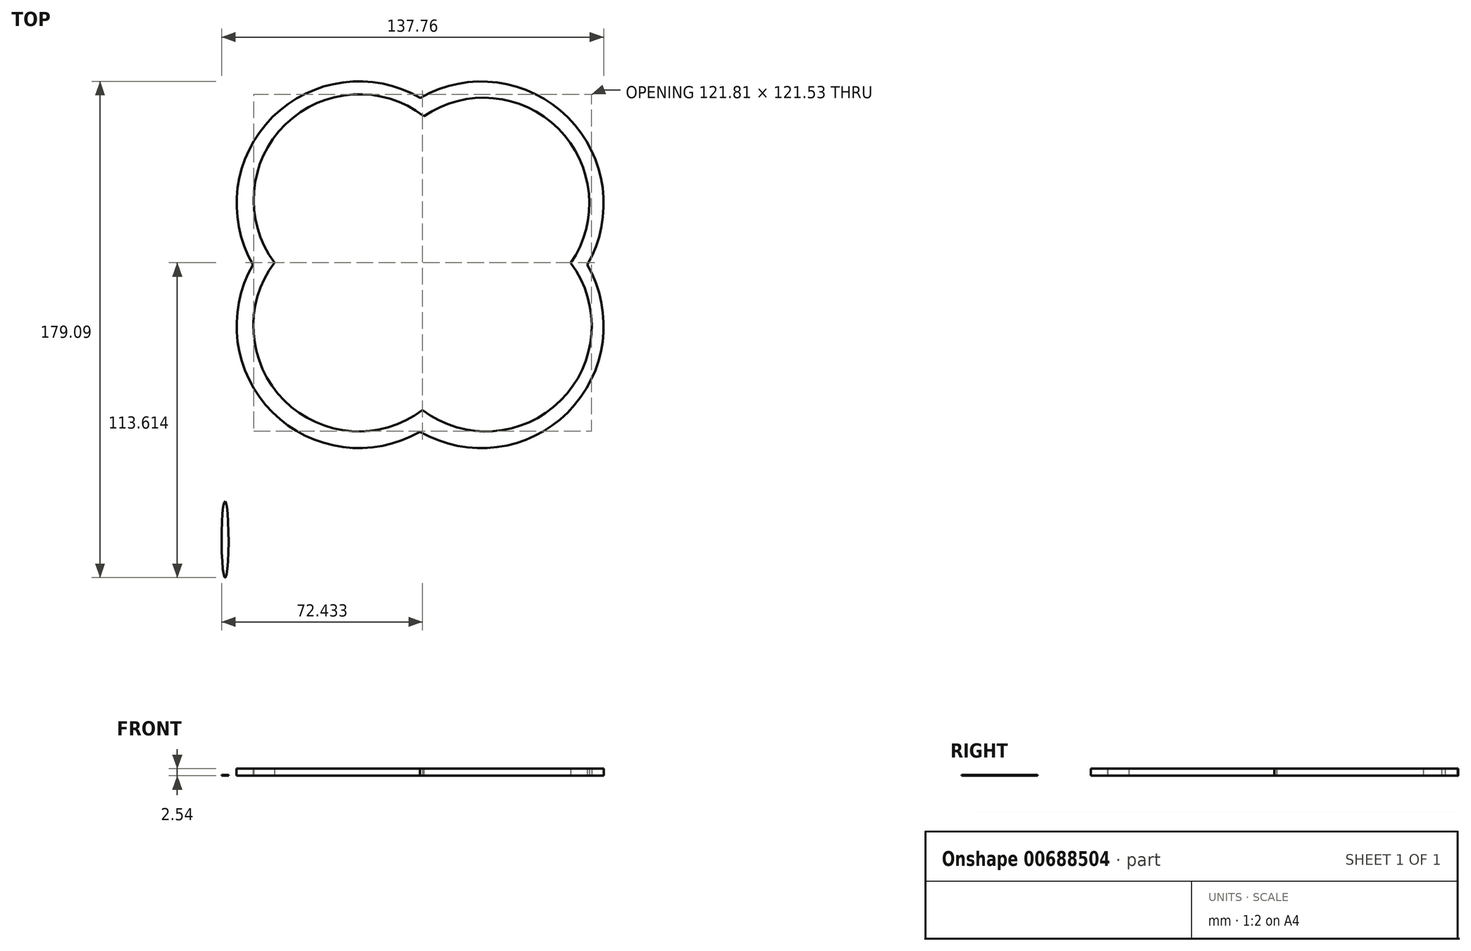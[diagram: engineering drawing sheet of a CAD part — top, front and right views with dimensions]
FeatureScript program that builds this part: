
annotation { "Feature Type Name" : "Feature", "Feature Type Description" : "" }
export const myFeature = defineFeature(function(context is Context, id is Id, definition is map)
    precondition{}
    {
        {
            var Q0;
            Q0=qCreatedBy(makeId("Top.planeOp"),FACE);
            var sketch = newSketch(context, id + "F0", { "sketchPlane" : qUnion([Q0])});
            skCircle(sketch, "E0", {"center": v(0, 44.12) * mm, "radius": 44.12 * mm});
            skCircle(sketch, "E1", {"center": v(44.12, 44.07) * mm, "radius": 44.12 * mm});
            skCircle(sketch, "E2", {"center": v(44.12, -0.05) * mm, "radius": 44.12 * mm});
            skCircle(sketch, "E3", {"center": v(0, 0) * mm, "radius": 44.12 * mm});
            skSolve(sketch);
        }
        {
            var Q0;
            {var subQ0=sQuery(id+"F0.wireOp",EDGE,"E3");var subQ1=sQuery(id+"F0.wireOp",EDGE,"E0");var subQ2=makeQuery(id+"F0.imprint","INTERSECT",VERTEX,{"disambiguationData":[OD(0.0)],"derivedFrom":[subQ1,subQ0]});Q0=makeQuery(id+"F0.imprint","IMPRINT",FACE,{"disambiguationData":[TD([[makeQuery(id+"F0.imprint","IMPRINT",EDGE,{"disambiguationData":[TD([[subQ2,1.0]])],"derivedFrom":subQ1}),1.0]])]});}
            var Q1;
            {var subQ0=sQuery(id+"F0.wireOp",EDGE,"E3");var subQ1=sQuery(id+"F0.wireOp",EDGE,"E0");var subQ2=makeQuery(id+"F0.imprint","INTERSECT",VERTEX,{"disambiguationData":[OD(0.0)],"derivedFrom":[subQ1,subQ0]});Q1=makeQuery(id+"F0.imprint","IMPRINT",FACE,{"disambiguationData":[TD([[makeQuery(id+"F0.imprint","IMPRINT",EDGE,{"disambiguationData":[TD([[subQ2,-1.0]])],"derivedFrom":subQ1}),1.0]])]});}
            var Q2;
            {var subQ0=sQuery(id+"F0.wireOp",EDGE,"E1");var subQ1=sQuery(id+"F0.wireOp",EDGE,"E0");var subQ2=makeQuery(id+"F0.imprint","INTERSECT",VERTEX,{"disambiguationData":[OD(0.0)],"derivedFrom":[subQ1,subQ0]});Q2=makeQuery(id+"F0.imprint","IMPRINT",FACE,{"disambiguationData":[TD([[makeQuery(id+"F0.imprint","IMPRINT",EDGE,{"disambiguationData":[TD([[subQ2,1.0]])],"derivedFrom":subQ1}),1.0]])]});}
            var Q3;
            {var subQ0=sQuery(id+"F0.wireOp",EDGE,"E3");var subQ1=sQuery(id+"F0.wireOp",EDGE,"E0");var subQ2=makeQuery(id+"F0.imprint","INTERSECT",VERTEX,{"disambiguationData":[OD(0.0)],"derivedFrom":[subQ1,subQ0]});Q3=makeQuery(id+"F0.imprint","IMPRINT",FACE,{"disambiguationData":[TD([[makeQuery(id+"F0.imprint","IMPRINT",EDGE,{"disambiguationData":[TD([[subQ2,-1.0]])],"derivedFrom":subQ1}),-1.0]])]});}
            var Q4;
            {var subQ0=sQuery(id+"F0.wireOp",EDGE,"E2");var subQ1=sQuery(id+"F0.wireOp",EDGE,"E0");var subQ2=makeQuery(id+"F0.imprint","INTERSECT",VERTEX,{"disambiguationData":[OD(0.0)],"derivedFrom":[subQ1,subQ0]});Q4=makeQuery(id+"F0.imprint","IMPRINT",FACE,{"disambiguationData":[TD([[makeQuery(id+"F0.imprint","IMPRINT",EDGE,{"disambiguationData":[TD([[subQ2,-1.0]])],"derivedFrom":subQ1}),-1.0]])]});}
            var Q5;
            {var subQ0=sQuery(id+"F0.wireOp",EDGE,"E2");var subQ1=sQuery(id+"F0.wireOp",EDGE,"E1");var subQ2=makeQuery(id+"F0.imprint","INTERSECT",VERTEX,{"disambiguationData":[OD(0.0)],"derivedFrom":[subQ1,subQ0]});Q5=makeQuery(id+"F0.imprint","IMPRINT",FACE,{"disambiguationData":[TD([[makeQuery(id+"F0.imprint","IMPRINT",EDGE,{"disambiguationData":[TD([[subQ2,1.0]])],"derivedFrom":subQ1}),-1.0]])]});}
            var Q6;
            {var subQ0=sQuery(id+"F0.wireOp",EDGE,"E1");var subQ1=sQuery(id+"F0.wireOp",EDGE,"E0");var subQ2=makeQuery(id+"F0.imprint","INTERSECT",VERTEX,{"disambiguationData":[OD(0.0)],"derivedFrom":[subQ1,subQ0]});Q6=makeQuery(id+"F0.imprint","IMPRINT",FACE,{"disambiguationData":[TD([[makeQuery(id+"F0.imprint","IMPRINT",EDGE,{"disambiguationData":[TD([[subQ2,1.0]])],"derivedFrom":subQ1}),-1.0]])]});}
            var Q7;
            {var subQ0=sQuery(id+"F0.wireOp",EDGE,"E3");var subQ1=sQuery(id+"F0.wireOp",EDGE,"E0");var subQ2=makeQuery(id+"F0.imprint","INTERSECT",VERTEX,{"disambiguationData":[OD(1.0)],"derivedFrom":[subQ1,subQ0]});Q7=makeQuery(id+"F0.imprint","IMPRINT",FACE,{"disambiguationData":[TD([[makeQuery(id+"F0.imprint","IMPRINT",EDGE,{"disambiguationData":[TD([[subQ2,-1.0]])],"derivedFrom":subQ1}),-1.0]])]});}
            extrude(context, id + "F1", {"entities" : qUnion([Q0, Q1, Q2, Q3, Q4, Q5, Q6, Q7]), "depth" : 2.54 * mm, "offsetDistance" : 25.4 * mm});
        }
        {
            var Q0;
            Q0=qCreatedBy(makeId("Top.planeOp"),FACE);
            var sketch = newSketch(context, id + "F2", { "sketchPlane" : qUnion([Q0])});
            skEllipse(sketch, "E4", {"center": v(44.96, 44.21) * mm, "majorRadius": 22.38 * mm, "minorRadius": 2.06 * mm, "majorAxis": v(-0.68, -0.74)});
            skSolve(sketch);
        }
        {
            var Q0;
            Q0=qCreatedBy(makeId("Top.planeOp"),FACE);
            var sketch = newSketch(context, id + "F3", { "sketchPlane" : qUnion([Q0])});
            skEllipse(sketch, "E5", {"center": v(45.81, 0) * mm, "majorRadius": 24.07 * mm, "minorRadius": 1.26 * mm, "majorAxis": v(0, 1)});
            skSolve(sketch);
        }
        {
            var Q0;
            Q0=qCreatedBy(makeId("Top.planeOp"),FACE);
            var sketch = newSketch(context, id + "F4", { "sketchPlane" : qUnion([Q0])});
            skPoint(sketch, "E6", {"position": v(65.34, 0) * mm});
            skPoint(sketch, "E7", {"position": v(65.34, 44.44) * mm});
            skPoint(sketch, "E8", {"position": v(0, 44.44) * mm});
            skPoint(sketch, "E9", {"position": v(0, 0) * mm});
            skPoint(sketch, "E10", {"position": v(-30.16, 44.44) * mm});
            skPoint(sketch, "E11", {"position": v(-31.21, 0) * mm});
            skPoint(sketch, "E12", {"position": v(0, 72.16) * mm});
            skPoint(sketch, "E13", {"position": v(44.36, 72.02) * mm});
            skPoint(sketch, "E14", {"position": v(0, -29.56) * mm});
            skPoint(sketch, "E15", {"position": v(50.9, -30.75) * mm});
            skSolve(sketch);
        }
        {
            var Q0;
            Q0=qCreatedBy(makeId("Top.planeOp"),FACE);
            var sketch = newSketch(context, id + "F5", { "sketchPlane" : qUnion([Q0])});
            skArc(sketch, "E16", {"start": v(-16.38, 20.5) * mm, "mid": v(26.17, 60.24) * mm, "end": v(-29.78, 44.16) * mm});
            skSolve(sketch);
        }
        {
            var Q0;
            Q0=sQuery(id+"F5.wireOp",VERTEX,"E16.center");
            var Q1;
            Q1=sQuery(id+"F3.wireOp",VERTEX,"E5.center");
            var Q2;
            Q2=sQuery(id+"F4.wireOp",VERTEX,"E9");
            var Q3;
            Q3=sQuery(id+"F2.wireOp",VERTEX,"E4.center");
            var Q4;
            Q4=makeQuery(id+"F1.opExtrude","SWEPT_BODY",BODY,{"disambiguationData":[OSD([sQuery(id+"F0.wireOp",EDGE,"E0"),sQuery(id+"F0.wireOp",EDGE,"E1"),sQuery(id+"F0.wireOp",EDGE,"E2"),sQuery(id+"F0.wireOp",EDGE,"E3")])]});
            hole(context, id + "F6", {"style" : HoleStyle.SIMPLE, "endStyle" : HoleEndStyle.THROUGH, "oppositeDirection" : true, "holeDiameter" : 76.2 * mm, "majorDiameter" : 6.35 * mm, "isTappedThrough" : true, "tappedDepth" : 12.7 * mm, "tapClearance" : 3, "locations" : qUnion([Q0, Q1, Q2, Q3]), "scope" : qUnion([Q4])});
        }
        {
            var Q0;
            Q0=qCreatedBy(makeId("Top.planeOp"),FACE);
            var sketch = newSketch(context, id + "F7", { "sketchPlane" : qUnion([Q0])});
            skEllipse(sketch, "E17", {"center": v(-48.28, -77.1) * mm, "majorRadius": 13.76 * mm, "minorRadius": 1.25 * mm, "majorAxis": v(0, 1)});
            skSolve(sketch);
        }
        {
            var Q0;
            Q0=makeQuery(id+"F7.imprint","IMPRINT",FACE,{"disambiguationData":[TD([[makeQuery(id+"F7.imprint","IMPRINT",EDGE,{"derivedFrom":sQuery(id+"F7.wireOp",EDGE,"E17")}),1.0]])]});
            extrude(context, id + "F8", {"entities" : qUnion([Q0]), "depth" : .32 * mm, "offsetDistance" : 25.4 * mm});
        }
    });
